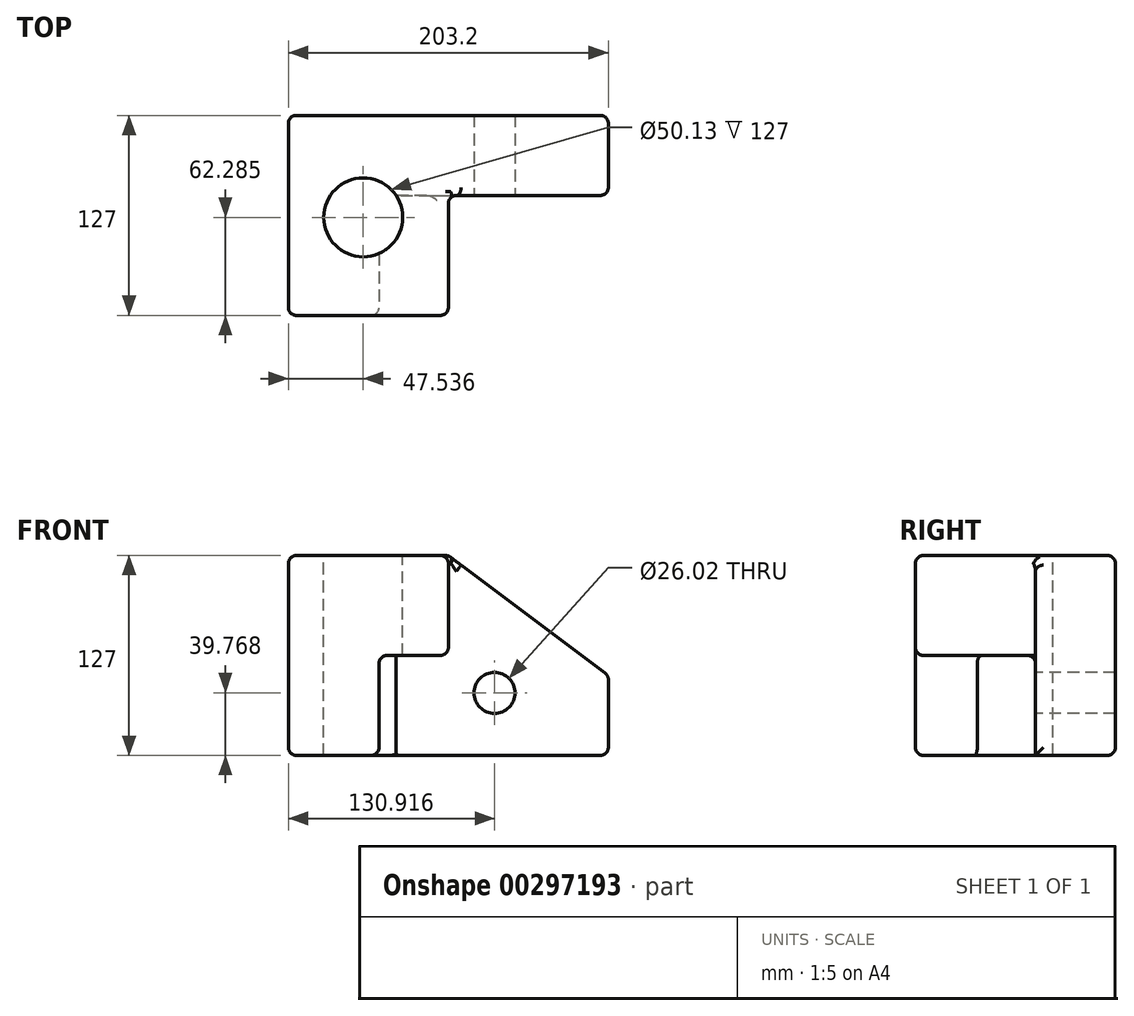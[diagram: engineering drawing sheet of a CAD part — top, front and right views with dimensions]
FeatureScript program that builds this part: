
annotation { "Feature Type Name" : "Feature", "Feature Type Description" : "" }
export const myFeature = defineFeature(function(context is Context, id is Id, definition is map)
    precondition{}
    {
        {
            var Q0;
            Q0=qCreatedBy(makeId("Front.planeOp"),FACE);
            var sketch = newSketch(context, id + "F0", { "sketchPlane" : qUnion([Q0])});
            skLineSegment(sketch, "E0.bottom", {"start": v(-101.6, -63.5) * mm, "end": v(101.6, -63.5) * mm});
            skLineSegment(sketch, "E0.top", {"start": v(-101.6, 63.5) * mm, "end": v(101.6, 63.5) * mm});
            skLineSegment(sketch, "E0.left", {"start": v(-101.6, -63.5) * mm, "end": v(-101.6, 63.5) * mm});
            skLineSegment(sketch, "E0.right", {"start": v(101.6, -63.5) * mm, "end": v(101.6, 63.5) * mm});
            skPoint(sketch, "E0.middle", {"position": v(0, 0) * mm});
            skSolve(sketch);
        }
        {
            var Q0;
            Q0 = qSketchRegion(id + "F0", true);
            extrude(context, id + "F1", {"entities" : qUnion([Q0]), "depth" : 127 * mm});
        }
        {
            var Q0;
            Q0=makeQuery(id+"F1.opExtrude","CAP_FACE",FACE,{"disambiguationData":[OSD([sQuery(id+"F0.wireOp",EDGE,"E0.bottom"),sQuery(id+"F0.wireOp",EDGE,"E0.top"),sQuery(id+"F0.wireOp",EDGE,"E0.left"),sQuery(id+"F0.wireOp",EDGE,"E0.right")])],"isStart":false});
            var sketch = newSketch(context, id + "F2", { "sketchPlane" : qUnion([Q0])});
            skLineSegment(sketch, "E1", {"start": v(-101.6, -63.5) * mm, "end": v(-101.6, 63.5) * mm});
            skLineSegment(sketch, "E2", {"start": v(-101.6, 63.5) * mm, "end": v(0, 63.5) * mm});
            skLineSegment(sketch, "E3", {"start": v(0, 63.5) * mm, "end": v(0, 0) * mm});
            skLineSegment(sketch, "E4", {"start": v(0, 0) * mm, "end": v(-44.04, 0) * mm});
            skPoint(sketch, "E4.endSnap0", {"position": v(-101.6, 0) * mm});
            skLineSegment(sketch, "E5", {"start": v(-44.04, 0) * mm, "end": v(-44.04, -63.5) * mm});
            skLineSegment(sketch, "E6", {"start": v(-44.04, -63.5) * mm, "end": v(-101.6, -63.5) * mm});
            skSolve(sketch);
        }
        {
            var Q0;
            {var subQ3=sQuery(id+"F2.wireOp",EDGE,"E3");Q0=makeQuery(id+"F2.imprint","IMPRINT",FACE,{"disambiguationData":[TD([[makeQuery(id+"F2.imprint","IMPRINT",EDGE,{"derivedFrom":subQ3}),1.0]])]});}
            extrude(context, id + "F3", {"entities" : qUnion([Q0]), "operationType" : NewBodyOperationType.REMOVE, "oppositeDirection" : true, "depth" : 76.2 * mm});
        }
        {
            var Q0;
            Q0=makeQuery(id+"F1.opExtrude","SWEPT_EDGE",EDGE,{"disambiguationData":[OSD([sQuery(id+"F0.wireOp",EDGE,"E0.top"),sQuery(id+"F0.wireOp",EDGE,"E0.right")])]});
            chamfer(context, id + "F4", {"entities" : qUnion([Q0]), "chamferType" : ChamferType.TWO_OFFSETS, "width1" : 76.2 * mm, "oppositeDirection" : true, "width2" : 101.6 * mm, "tangentPropagation" : true});
        }
        {
            var Q0;
            Q0=makeQuery(id+"F1.opExtrude","CAP_EDGE",EDGE,{"disambiguationData":[OSD([sQuery(id+"F0.wireOp",EDGE,"E0.top")])],"isStart":false});
            var Q1;
            Q1=makeQuery(id+"F1.opExtrude","SWEPT_FACE",FACE,{"disambiguationData":[OSD([sQuery(id+"F0.wireOp",EDGE,"E0.top")])]});
            var Q2;
            Q2=makeQuery(id+"F4.opChamfer","BLEND_FACE",FACE,{"disambiguationData":[OSD([sQuery(id+"F0.wireOp",EDGE,"E0.top"),sQuery(id+"F0.wireOp",EDGE,"E0.right")])]});
            var Q3;
            Q3=makeQuery(id+"F3.boolean.opBoolean","COPY",FACE,{"derivedFrom":makeQuery(id+"F3.opExtrude","SWEPT_FACE",FACE,{"disambiguationData":[OSD([sQuery(id+"F2.wireOp",EDGE,"E3")])]})});
            var Q4;
            Q4=makeQuery(id+"F1.opExtrude","SWEPT_FACE",FACE,{"disambiguationData":[OSD([sQuery(id+"F0.wireOp",EDGE,"E0.right")])]});
            var Q5;
            Q5=makeQuery(id+"F3.boolean.opBoolean","COPY",FACE,{"derivedFrom":makeQuery(id+"F3.opExtrude","SWEPT_FACE",FACE,{"disambiguationData":[OSD([sQuery(id+"F2.wireOp",EDGE,"E5")])]})});
            var Q6;
            Q6=makeQuery(id+"F1.opExtrude","CAP_FACE",FACE,{"disambiguationData":[OSD([sQuery(id+"F0.wireOp",EDGE,"E0.bottom"),sQuery(id+"F0.wireOp",EDGE,"E0.top"),sQuery(id+"F0.wireOp",EDGE,"E0.left"),sQuery(id+"F0.wireOp",EDGE,"E0.right")])],"isStart":false});
            var Q7;
            Q7=makeQuery(id+"F1.opExtrude","CAP_EDGE",EDGE,{"disambiguationData":[OSD([sQuery(id+"F0.wireOp",EDGE,"E0.left")])],"isStart":true});
            var Q8;
            Q8=makeQuery(id+"F1.opExtrude","CAP_EDGE",EDGE,{"disambiguationData":[OSD([sQuery(id+"F0.wireOp",EDGE,"E0.bottom")])],"isStart":true});
            var Q9;
            Q9=makeQuery(id+"F1.opExtrude","SWEPT_EDGE",EDGE,{"disambiguationData":[OSD([sQuery(id+"F0.wireOp",EDGE,"E0.bottom"),sQuery(id+"F0.wireOp",EDGE,"E0.left")])]});
            fillet(context, id + "F5", {"entities" : qUnion([Q0, Q1, Q2, Q3, Q4, Q5, Q6, Q7, Q8, Q9]), "radius" : 5.08 * mm, "tangentPropagation" : true, "allowEdgeOverflow" : false});
        }
        {
            var Q0;
            Q0=makeQuery(id+"F3.boolean.opBoolean","COPY",FACE,{"derivedFrom":makeQuery(id+"F3.opExtrude","CAP_FACE",FACE,{"disambiguationData":[OSD([sQuery(id+"F0.wireOp",EDGE,"E0.bottom"),sQuery(id+"F0.wireOp",EDGE,"E0.top"),sQuery(id+"F0.wireOp",EDGE,"E0.right"),sQuery(id+"F2.wireOp",EDGE,"E3"),sQuery(id+"F2.wireOp",EDGE,"E4"),sQuery(id+"F2.wireOp",EDGE,"E5")])],"isStart":false})});
            var sketch = newSketch(context, id + "F6", { "sketchPlane" : qUnion([Q0])});
            skCircle(sketch, "E7", {"center": v(29.32, -23.73) * mm, "radius": 13.01 * mm});
            skSolve(sketch);
        }
        {
            var Q0;
            Q0 = qSketchRegion(id + "F6", true);
            var Q1;
            Q1=makeQuery(id+"F1.opExtrude","CAP_FACE",FACE,{"disambiguationData":[OSD([sQuery(id+"F0.wireOp",EDGE,"E0.bottom"),sQuery(id+"F0.wireOp",EDGE,"E0.top"),sQuery(id+"F0.wireOp",EDGE,"E0.left"),sQuery(id+"F0.wireOp",EDGE,"E0.right")])],"isStart":true});
            extrude(context, id + "F7", {"entities" : qUnion([Q0]), "operationType" : NewBodyOperationType.REMOVE, "endBound" : BoundingType.UP_TO_SURFACE, "oppositeDirection" : true, "endBoundEntityFace" : qUnion([Q1]), "depth" : 25.4 * mm});
        }
        {
            var Q0;
            Q0=makeQuery(id+"F1.opExtrude","SWEPT_FACE",FACE,{"disambiguationData":[OSD([sQuery(id+"F0.wireOp",EDGE,"E0.top")])]});
            var sketch = newSketch(context, id + "F8", { "sketchPlane" : qUnion([Q0])});
            skCircle(sketch, "E8", {"center": v(-54.06, -64.72) * mm, "radius": 25.06 * mm});
            skSolve(sketch);
        }
        {
            var Q0;
            Q0 = qSketchRegion(id + "F8", true);
            extrude(context, id + "F9", {"entities" : qUnion([Q0]), "operationType" : NewBodyOperationType.REMOVE, "endBound" : BoundingType.THROUGH_ALL, "oppositeDirection" : true, "depth" : 25.4 * mm});
        }
    });
